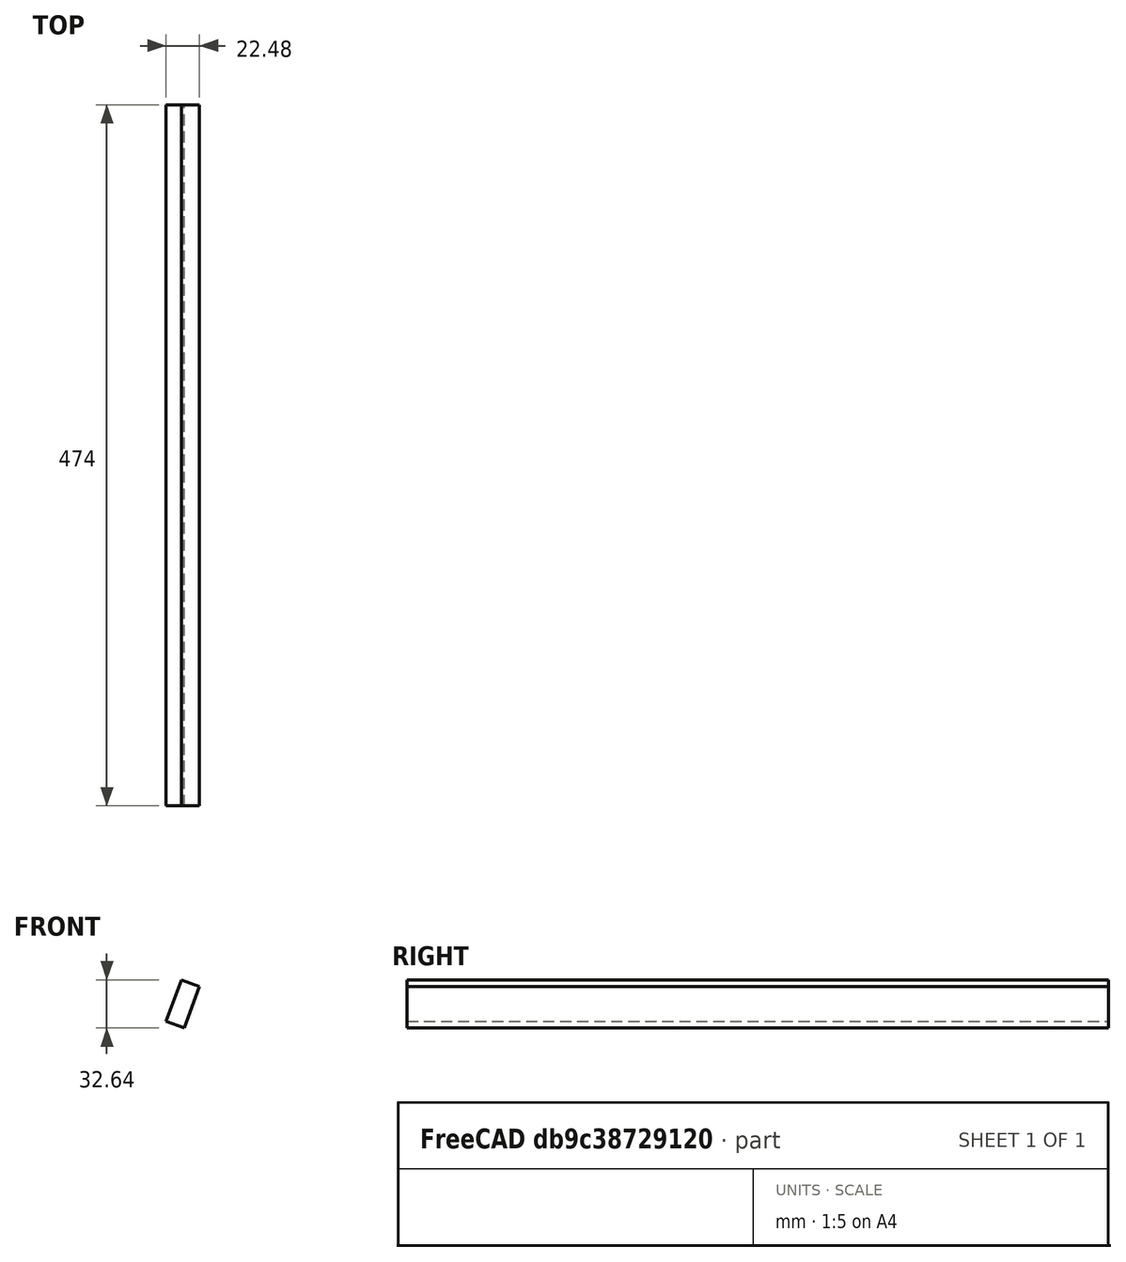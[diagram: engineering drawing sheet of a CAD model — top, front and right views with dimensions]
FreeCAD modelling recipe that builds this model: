
FCSTD DOCUMENT  (FreeCAD 0.18R14555 (Git shallow))
Label: 4000_Body_front_top_YZ
License: All rights reserved
LicenseURL: http://en.wikipedia.org/wiki/All_rights_reserved
objects: Spreadsheet::Sheet×1, Sketcher::SketchObject×1, PartDesign::Pad×1, PartDesign::Body×1
note: 4 computed .brp shape members not serialized (recipe doc carries the construction recipe); baked Part::Feature solids carry a one-line shape summary decoded from their .brp

FEATURE [Spreadsheet::Sheet] Spreadsheet  label="xls"
  cells = B5=BODY FRONT; E5=nominal size; B6=Board Thickness; C6(thickness)=13; D6=xls.thickness; B7=Horizontal Y; C7(width)==+E7 - 2 * C6; D7=xls.width; E7=500; B8=X=; C8(height)=30; D8=xls.height; B9=Angle Y; C9(tilt)=70; D9=xls.tilt
FEATURE [Sketcher::SketchObject] Sketch
  MapMode = 5
  Placement = pos=(0,0,0) rot=(1,0,0;1.5708rad)
  Support = -> [XZ_Plane]
  expr: Constraints[7] = xls.tilt
  expr: Constraints[6] = xls.height
  expr: Constraints[5] = xls.thickness
  sketch-geometry (4):
    g0: LineSegment StartX=0 StartY=0 StartZ=0 EndX=10.2606 EndY=28.1908 EndZ=0
    g1: LineSegment StartX=10.2606 StartY=28.1908 StartZ=0 EndX=22.4766 EndY=23.7445 EndZ=0
    g2: LineSegment StartX=22.4766 StartY=23.7445 StartZ=0 EndX=12.216 EndY=-4.44626 EndZ=0
    g3: LineSegment StartX=12.216 StartY=-4.44626 StartZ=0 EndX=0 EndY=0 EndZ=0
  constraints (11):
    c: Coincident(g0,g1)
    c: Coincident(g1,g2)
    c: Parallel(g3,g1)
    c: Parallel(g0,g2)
    c: Perpendicular(g0,g3)
    c: Distance(g3) = 13
    c: Distance(g0) = 30
    c: Angle(g-1,g0) = 1.22173
    c: Coincident(g0,g3)
    c: Coincident(g3,g2)
    c: Coincident(g0,g-1)
FEATURE [PartDesign::Pad] Pad
  Length = 474
  Length2 = 100
  Placement = pos=(0,0,0) rot=(1,0,0;1.5708rad)
  Profile = -> Sketch
  Reversed = true
  Type = 0
  expr: Length = xls.width
FEATURE [PartDesign::Body] Body
  Group = -> [Sketch,Pad]
  Origin = -> Origin
  Tip = -> Pad
